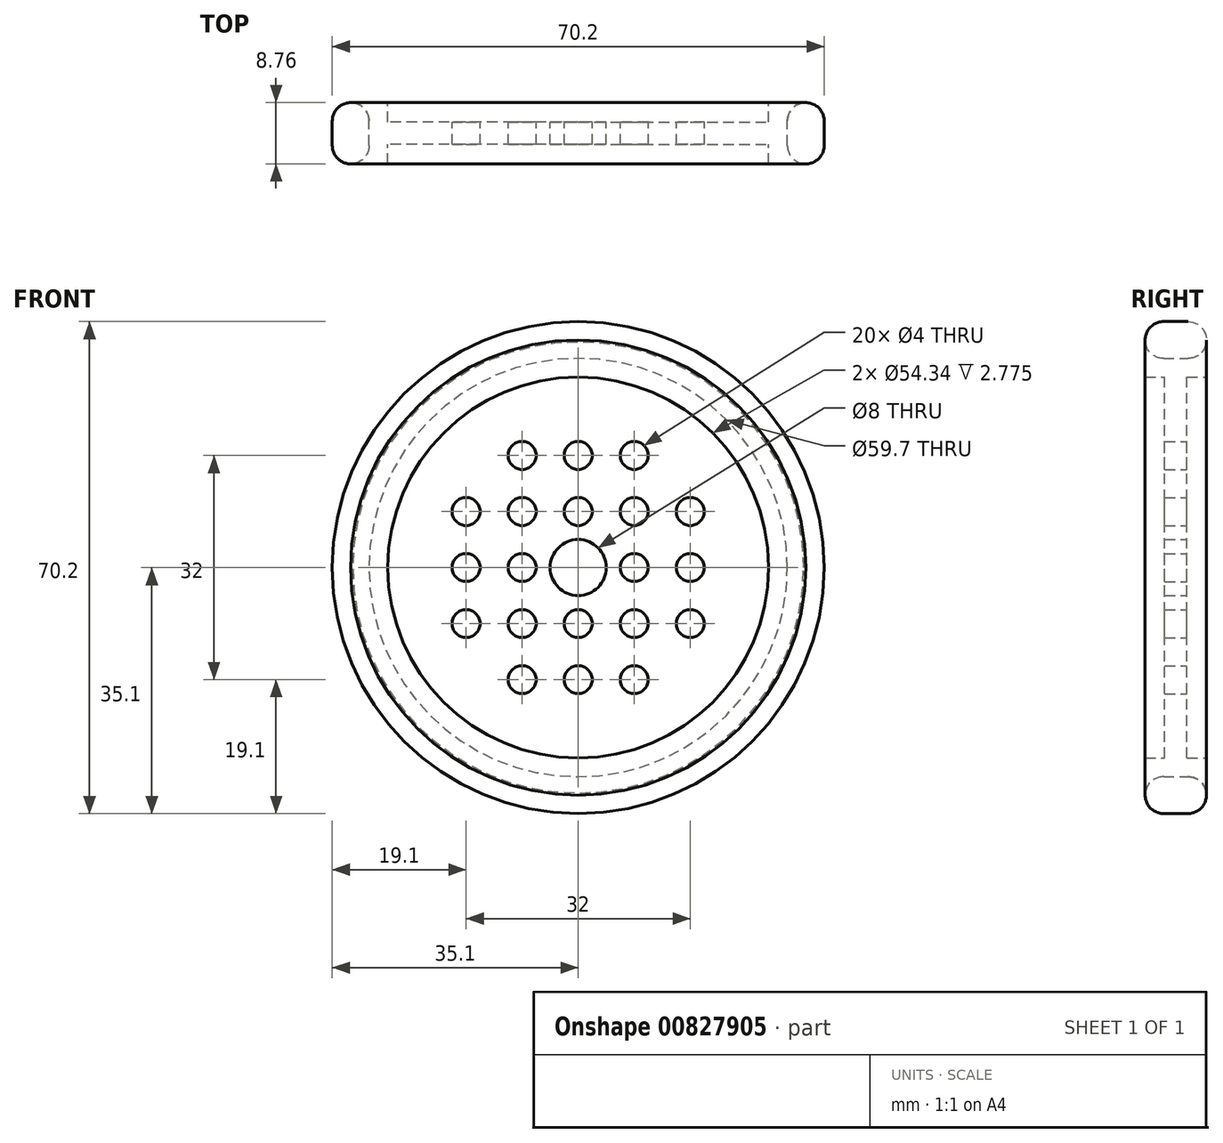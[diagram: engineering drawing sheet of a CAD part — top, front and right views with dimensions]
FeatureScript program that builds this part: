
annotation { "Feature Type Name" : "Feature", "Feature Type Description" : "" }
export const myFeature = defineFeature(function(context is Context, id is Id, definition is map)
    precondition{}
    {
        {
            var Q0;
            Q0=qCreatedBy(makeId("Right.planeOp"),FACE);
            var sketch = newSketch(context, id + "F0", { "sketchPlane" : qUnion([Q0])});
            skLineSegment(sketch, "E0.bottom", {"start": v(1.75, 35.1) * mm, "end": v(-1.75, 35.1) * mm});
            skLineSegment(sketch, "E0.top", {"start": v(1.75, 29.85) * mm, "end": v(-1.75, 29.85) * mm});
            skPoint(sketch, "E0.middle", {"position": v(0, 32.48) * mm});
            skArc(sketch, "E1", {"start": v(1.75, 29.85) * mm, "mid": v(4.38, 32.48) * mm, "end": v(1.75, 35.1) * mm});
            skArc(sketch, "E2", {"start": v(-1.75, 35.1) * mm, "mid": v(-4.38, 32.48) * mm, "end": v(-1.75, 29.85) * mm});
            skLineSegment(sketch, "E3", {"start": v(0, 0) * mm, "end": v(-9.37, 0) * mm, "construction": true});
            skLineSegment(sketch, "E4", {"start": v(-4.38, 32.48) * mm, "end": v(4.37, 32.48) * mm, "construction": true});
            skSolve(sketch);
        }
        {
            var Q0;
            Q0=qSketchRegion(id+"F0",true);
            var Q1;
            Q1=sQuery(id+"F0.wireOp",EDGE,"E3");
            revolve(context, id + "F1", {"surfaceOperationType" : NewSurfaceOperationType.NEW, "entities" : qUnion([Q0]), "axis" : qUnion([Q1]), "revolveType" : RevolveType.FULL});
        }
        {
            var Q0;
            Q0=qCreatedBy(makeId("Right.planeOp"),FACE);
            var sketch = newSketch(context, id + "F2", { "sketchPlane" : qUnion([Q0])});
            skLineSegment(sketch, "E5", {"start": v(0.72, 0) * mm, "end": v(-12.76, 0) * mm, "construction": true});
            skArc(sketch, "E6", {"start": v(1.75, 29.85) * mm, "mid": v(3.5, 30.51) * mm, "end": v(4.36, 32.17) * mm});
            skArc(sketch, "E7", {"start": v(4.38, -32.48) * mm, "mid": v(3.6, -30.62) * mm, "end": v(1.75, -29.85) * mm});
            skArc(sketch, "E8", {"start": v(-4.38, 32.48) * mm, "mid": v(-3.6, 30.62) * mm, "end": v(-1.75, 29.85) * mm});
            skLineSegment(sketch, "E9", {"start": v(-1.75, 29.85) * mm, "end": v(1.75, 29.85) * mm});
            skLineSegment(sketch, "E10", {"start": v(-4.38, 32.48) * mm, "end": v(-4.38, -32.48) * mm, "construction": true});
            skLineSegment(sketch, "E11", {"start": v(4.38, 32.48) * mm, "end": v(4.38, -32.48) * mm, "construction": true});
            skLineSegment(sketch, "E12", {"start": v(-4.38, 32.48) * mm, "end": v(-4.38, 27.17) * mm});
            skLineSegment(sketch, "E13", {"start": v(-4.38, 27.17) * mm, "end": v(4.38, 27.17) * mm});
            skLineSegment(sketch, "E14", {"start": v(4.37, 27.17) * mm, "end": v(4.36, 32.17) * mm});
            skSolve(sketch);
        }
        {
            var Q0;
            Q0=qSketchRegion(id+"F2",true);
            var Q1;
            Q1=sQuery(id+"F2.wireOp",EDGE,"E5");
            revolve(context, id + "F3", {"surfaceOperationType" : NewSurfaceOperationType.NEW, "entities" : qUnion([Q0]), "axis" : qUnion([Q1]), "revolveType" : RevolveType.FULL});
        }
        {
            var Q0;
            Q0=qCreatedBy(makeId("Front.planeOp"),FACE);
            var sketch = newSketch(context, id + "F4", { "sketchPlane" : qUnion([Q0])});
            skCircle(sketch, "E15.0", {"center": v(0, 0) * mm, "radius": 27.17 * mm});
            skCircle(sketch, "E16", {"center": v(0, 0) * mm, "radius": 4 * mm});
            skLineSegment(sketch, "E17.bottom", {"start": v(8, 8) * mm, "end": v(-8, 8) * mm, "construction": true});
            skLineSegment(sketch, "E17.top", {"start": v(8, -8) * mm, "end": v(-8, -8) * mm, "construction": true});
            skLineSegment(sketch, "E17.left", {"start": v(8, 8) * mm, "end": v(8, -8) * mm, "construction": true});
            skLineSegment(sketch, "E17.right", {"start": v(-8, 8) * mm, "end": v(-8, -8) * mm, "construction": true});
            skCircle(sketch, "E18", {"center": v(-8, 8) * mm, "radius": 2 * mm});
            skCircle(sketch, "E19", {"center": v(8, 8) * mm, "radius": 2 * mm});
            skCircle(sketch, "E20", {"center": v(8, -8) * mm, "radius": 2 * mm});
            skCircle(sketch, "E21", {"center": v(-8, -8) * mm, "radius": 2 * mm});
            skCircle(sketch, "E22", {"center": v(8, 0) * mm, "radius": 2 * mm});
            skCircle(sketch, "E23", {"center": v(-8, 0) * mm, "radius": 2 * mm});
            skCircle(sketch, "E24", {"center": v(0, 8) * mm, "radius": 2 * mm});
            skCircle(sketch, "E25", {"center": v(0, -8) * mm, "radius": 2 * mm});
            skLineSegment(sketch, "E26.bottom", {"start": v(8, 16) * mm, "end": v(-8, 16) * mm, "construction": true});
            skLineSegment(sketch, "E26.top", {"start": v(8, -16) * mm, "end": v(-8, -16) * mm, "construction": true});
            skLineSegment(sketch, "E26.left", {"start": v(8, 16) * mm, "end": v(8, -16) * mm, "construction": true});
            skLineSegment(sketch, "E26.right", {"start": v(-8, 16) * mm, "end": v(-8, -16) * mm, "construction": true});
            skCircle(sketch, "E27", {"center": v(-8, 16) * mm, "radius": 2 * mm});
            skCircle(sketch, "E28", {"center": v(0, 16) * mm, "radius": 2 * mm});
            skCircle(sketch, "E29", {"center": v(8, 16) * mm, "radius": 2 * mm});
            skCircle(sketch, "E30.1.0", {"center": v(-16, -8) * mm, "radius": 2 * mm});
            skCircle(sketch, "E30.1.1", {"center": v(-16, 0) * mm, "radius": 2 * mm});
            skCircle(sketch, "E30.1.2", {"center": v(-16, 8) * mm, "radius": 2 * mm});
            skCircle(sketch, "E30.2.0", {"center": v(8, -16) * mm, "radius": 2 * mm});
            skCircle(sketch, "E30.2.1", {"center": v(0, -16) * mm, "radius": 2 * mm});
            skCircle(sketch, "E30.2.2", {"center": v(-8, -16) * mm, "radius": 2 * mm});
            skCircle(sketch, "E30.3.0", {"center": v(16, 8) * mm, "radius": 2 * mm});
            skCircle(sketch, "E30.3.1", {"center": v(16, 0) * mm, "radius": 2 * mm});
            skCircle(sketch, "E30.3.2", {"center": v(16, -8) * mm, "radius": 2 * mm});
            skSolve(sketch);
        }
        {
            var Q0;
            Q0 = qSketchRegion(id + "F4", true);
            extrude(context, id + "F5", {"entities" : qUnion([Q0]), "operationType" : NewBodyOperationType.ADD, "endBound" : BoundingType.SYMMETRIC, "depth" : 3.2 * mm, "offsetDistance" : 25 * mm});
        }
    });
